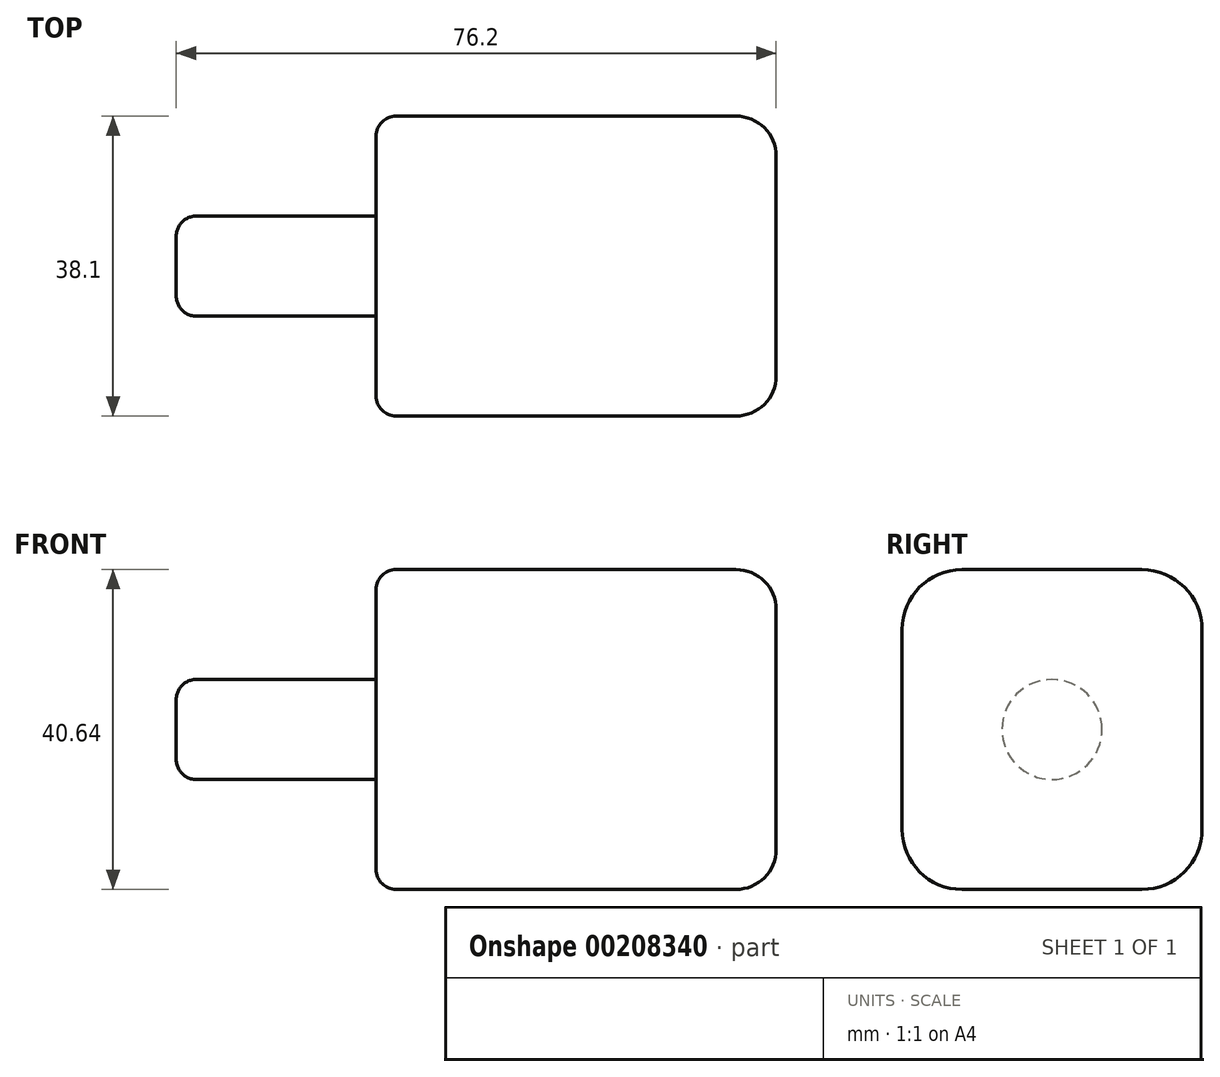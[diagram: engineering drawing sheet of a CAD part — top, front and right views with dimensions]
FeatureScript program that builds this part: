
annotation { "Feature Type Name" : "Feature", "Feature Type Description" : "" }
export const myFeature = defineFeature(function(context is Context, id is Id, definition is map)
    precondition{}
    {
        {
            var Q0;
            Q0=qCreatedBy(makeId("Right.planeOp"),FACE);
            var sketch = newSketch(context, id + "F0", { "sketchPlane" : qUnion([Q0])});
            skLineSegment(sketch, "E0.bottom", {"start": v(-15.1, 19.7) * mm, "end": v(23, 19.7) * mm});
            skLineSegment(sketch, "E0.top", {"start": v(-15.1, -20.93) * mm, "end": v(23, -20.93) * mm});
            skLineSegment(sketch, "E0.left", {"start": v(-15.1, 19.7) * mm, "end": v(-15.1, -20.93) * mm});
            skLineSegment(sketch, "E0.right", {"start": v(23, 19.7) * mm, "end": v(23, -20.93) * mm});
            skSolve(sketch);
        }
        {
            var Q0;
            Q0=makeQuery(id+"F0.imprint","IMPRINT",FACE,{"disambiguationData":[TD([[makeQuery(id+"F0.imprint","IMPRINT",EDGE,{"derivedFrom":sQuery(id+"F0.wireOp",EDGE,"E0.bottom")}),-1.0]])]});
            extrude(context, id + "F1", {"entities" : qUnion([Q0]), "depth" : 50.8 * mm});
        }
        {
            var Q0;
            Q0=makeQuery(id+"F1.opExtrude","CAP_FACE",FACE,{"disambiguationData":[OSD([sQuery(id+"F0.wireOp",EDGE,"E0.bottom"),sQuery(id+"F0.wireOp",EDGE,"E0.top"),sQuery(id+"F0.wireOp",EDGE,"E0.left"),sQuery(id+"F0.wireOp",EDGE,"E0.right")])],"isStart":true});
            var sketch = newSketch(context, id + "F2", { "sketchPlane" : qUnion([Q0])});
            skLineSegment(sketch, "E1", {"start": v(-23, -0.61) * mm, "end": v(15.1, -0.61) * mm});
            skLineSegment(sketch, "E2", {"start": v(-3.96, 19.7) * mm, "end": v(-3.96, -20.93) * mm});
            skCircle(sketch, "E3", {"center": v(-3.96, -0.61) * mm, "radius": 6.35 * mm});
            skSolve(sketch);
        }
        {
            var Q0;
            {var subQ0=sQuery(id+"F2.wireOp",EDGE,"E3");var subQ1=sQuery(id+"F2.wireOp",EDGE,"E1");var subQ2=makeQuery(id+"F2.imprint","INTERSECT",VERTEX,{"disambiguationData":[OD(0.0)],"derivedFrom":[subQ1,subQ0]});Q0=makeQuery(id+"F2.imprint","IMPRINT",FACE,{"disambiguationData":[TD([[makeQuery(id+"F2.imprint","IMPRINT",EDGE,{"disambiguationData":[TD([[subQ2,-1.0]])],"derivedFrom":subQ1}),-1.0]])]});}
            var Q1;
            {var subQ0=sQuery(id+"F2.wireOp",EDGE,"E2");var subQ1=sQuery(id+"F2.wireOp",EDGE,"E1");var subQ2=makeQuery(id+"F2.imprint","INTERSECT",VERTEX,{"derivedFrom":[subQ1,subQ0]});Q1=makeQuery(id+"F2.imprint","IMPRINT",FACE,{"disambiguationData":[TD([[makeQuery(id+"F2.imprint","IMPRINT",EDGE,{"disambiguationData":[TD([[subQ2,-1.0]])],"derivedFrom":subQ1}),-1.0]])]});}
            var Q2;
            {var subQ0=sQuery(id+"F2.wireOp",EDGE,"E3");var subQ1=sQuery(id+"F2.wireOp",EDGE,"E1");var subQ2=makeQuery(id+"F2.imprint","INTERSECT",VERTEX,{"disambiguationData":[OD(0.0)],"derivedFrom":[subQ1,subQ0]});Q2=makeQuery(id+"F2.imprint","IMPRINT",FACE,{"disambiguationData":[TD([[makeQuery(id+"F2.imprint","IMPRINT",EDGE,{"disambiguationData":[TD([[subQ2,-1.0]])],"derivedFrom":subQ1}),1.0]])]});}
            var Q3;
            {var subQ0=sQuery(id+"F2.wireOp",EDGE,"E2");var subQ1=sQuery(id+"F2.wireOp",EDGE,"E1");var subQ2=makeQuery(id+"F2.imprint","INTERSECT",VERTEX,{"derivedFrom":[subQ1,subQ0]});Q3=makeQuery(id+"F2.imprint","IMPRINT",FACE,{"disambiguationData":[TD([[makeQuery(id+"F2.imprint","IMPRINT",EDGE,{"disambiguationData":[TD([[subQ2,-1.0]])],"derivedFrom":subQ1}),1.0]])]});}
            extrude(context, id + "F3", {"entities" : qUnion([Q0, Q1, Q2, Q3]), "operationType" : NewBodyOperationType.ADD, "depth" : 25.4 * mm});
        }
        {
            var Q0;
            Q0=makeQuery(id+"F1.opExtrude","SWEPT_EDGE",EDGE,{"disambiguationData":[OSD([sQuery(id+"F0.wireOp",EDGE,"E0.top"),sQuery(id+"F0.wireOp",EDGE,"E0.right")])]});
            var Q1;
            Q1=makeQuery(id+"F1.opExtrude","SWEPT_EDGE",EDGE,{"disambiguationData":[OSD([sQuery(id+"F0.wireOp",EDGE,"E0.top"),sQuery(id+"F0.wireOp",EDGE,"E0.left")])]});
            var Q2;
            Q2=makeQuery(id+"F1.opExtrude","SWEPT_EDGE",EDGE,{"disambiguationData":[OSD([sQuery(id+"F0.wireOp",EDGE,"E0.bottom"),sQuery(id+"F0.wireOp",EDGE,"E0.left")])]});
            var Q3;
            Q3=makeQuery(id+"F1.opExtrude","SWEPT_EDGE",EDGE,{"disambiguationData":[OSD([sQuery(id+"F0.wireOp",EDGE,"E0.bottom"),sQuery(id+"F0.wireOp",EDGE,"E0.right")])]});
            fillet(context, id + "F4", {"entities" : qUnion([Q0, Q1, Q2, Q3]), "radius" : 7.62 * mm, "tangentPropagation" : true, "allowEdgeOverflow" : false});
        }
        {
            var Q0;
            Q0=makeQuery(id+"F1.opExtrude","CAP_EDGE",EDGE,{"disambiguationData":[OSD([sQuery(id+"F0.wireOp",EDGE,"E0.top")])],"isStart":true});
            fillet(context, id + "F5", {"entities" : qUnion([Q0]), "radius" : 2.54 * mm, "tangentPropagation" : true, "allowEdgeOverflow" : false});
        }
        {
            var Q0;
            Q0=makeQuery(id+"F3.opExtrude","CAP_FACE",FACE,{"disambiguationData":[OSD([sQuery(id+"F2.wireOp",EDGE,"E3")])],"isStart":false});
            fillet(context, id + "F6", {"entities" : qUnion([Q0]), "radius" : 2.54 * mm, "tangentPropagation" : true, "allowEdgeOverflow" : false});
        }
        {
            var Q0;
            Q0=makeQuery(id+"F1.opExtrude","CAP_EDGE",EDGE,{"disambiguationData":[OSD([sQuery(id+"F0.wireOp",EDGE,"E0.bottom")])],"isStart":false});
            var Q1;
            {var subQ0=sQuery(id+"F0.wireOp",EDGE,"E0.left");var subQ1=sQuery(id+"F0.wireOp",EDGE,"E0.bottom");Q1=makeQuery(id+"F4.opFillet","BLEND_EDGE",EDGE,{"blendedFrom":[makeQuery(id+"F1.opExtrude","SWEPT_EDGE",EDGE,{"disambiguationData":[OSD([subQ1,subQ0])]}),makeQuery(id+"F1.opExtrude","CAP_FACE",FACE,{"disambiguationData":[OSD([subQ1,sQuery(id+"F0.wireOp",EDGE,"E0.top"),subQ0,sQuery(id+"F0.wireOp",EDGE,"E0.right")])],"isStart":false})],"blendedInto":[makeQuery(id+"F1.opExtrude","CAP_FACE",FACE,{"disambiguationData":[OSD([subQ1,sQuery(id+"F0.wireOp",EDGE,"E0.top"),subQ0,sQuery(id+"F0.wireOp",EDGE,"E0.right")])],"isStart":false})]});}
            var Q2;
            Q2=makeQuery(id+"F1.opExtrude","CAP_EDGE",EDGE,{"disambiguationData":[OSD([sQuery(id+"F0.wireOp",EDGE,"E0.left")])],"isStart":false});
            var Q3;
            {var subQ0=sQuery(id+"F0.wireOp",EDGE,"E0.left");var subQ1=sQuery(id+"F0.wireOp",EDGE,"E0.top");Q3=makeQuery(id+"F4.opFillet","BLEND_EDGE",EDGE,{"blendedFrom":[makeQuery(id+"F1.opExtrude","SWEPT_EDGE",EDGE,{"disambiguationData":[OSD([subQ1,subQ0])]}),makeQuery(id+"F1.opExtrude","CAP_FACE",FACE,{"disambiguationData":[OSD([sQuery(id+"F0.wireOp",EDGE,"E0.bottom"),subQ1,subQ0,sQuery(id+"F0.wireOp",EDGE,"E0.right")])],"isStart":false})],"blendedInto":[makeQuery(id+"F1.opExtrude","CAP_FACE",FACE,{"disambiguationData":[OSD([sQuery(id+"F0.wireOp",EDGE,"E0.bottom"),subQ1,subQ0,sQuery(id+"F0.wireOp",EDGE,"E0.right")])],"isStart":false})]});}
            var Q4;
            Q4=makeQuery(id+"F1.opExtrude","CAP_EDGE",EDGE,{"disambiguationData":[OSD([sQuery(id+"F0.wireOp",EDGE,"E0.top")])],"isStart":false});
            var Q5;
            Q5=makeQuery(id+"F1.opExtrude","CAP_EDGE",EDGE,{"disambiguationData":[OSD([sQuery(id+"F0.wireOp",EDGE,"E0.right")])],"isStart":false});
            var Q6;
            {var subQ0=sQuery(id+"F0.wireOp",EDGE,"E0.right");var subQ1=sQuery(id+"F0.wireOp",EDGE,"E0.bottom");Q6=makeQuery(id+"F4.opFillet","BLEND_EDGE",EDGE,{"blendedFrom":[makeQuery(id+"F1.opExtrude","SWEPT_EDGE",EDGE,{"disambiguationData":[OSD([subQ1,subQ0])]}),makeQuery(id+"F1.opExtrude","CAP_FACE",FACE,{"disambiguationData":[OSD([subQ1,sQuery(id+"F0.wireOp",EDGE,"E0.top"),sQuery(id+"F0.wireOp",EDGE,"E0.left"),subQ0])],"isStart":false})],"blendedInto":[makeQuery(id+"F1.opExtrude","CAP_FACE",FACE,{"disambiguationData":[OSD([subQ1,sQuery(id+"F0.wireOp",EDGE,"E0.top"),sQuery(id+"F0.wireOp",EDGE,"E0.left"),subQ0])],"isStart":false})]});}
            var Q7;
            {var subQ0=sQuery(id+"F0.wireOp",EDGE,"E0.right");var subQ1=sQuery(id+"F0.wireOp",EDGE,"E0.top");Q7=makeQuery(id+"F4.opFillet","BLEND_EDGE",EDGE,{"blendedFrom":[makeQuery(id+"F1.opExtrude","SWEPT_EDGE",EDGE,{"disambiguationData":[OSD([subQ1,subQ0])]}),makeQuery(id+"F1.opExtrude","CAP_FACE",FACE,{"disambiguationData":[OSD([sQuery(id+"F0.wireOp",EDGE,"E0.bottom"),subQ1,sQuery(id+"F0.wireOp",EDGE,"E0.left"),subQ0])],"isStart":false})],"blendedInto":[makeQuery(id+"F1.opExtrude","CAP_FACE",FACE,{"disambiguationData":[OSD([sQuery(id+"F0.wireOp",EDGE,"E0.bottom"),subQ1,sQuery(id+"F0.wireOp",EDGE,"E0.left"),subQ0])],"isStart":false})]});}
            fillet(context, id + "F7", {"entities" : qUnion([Q0, Q1, Q2, Q3, Q4, Q5, Q6, Q7]), "radius" : 5.08 * mm, "tangentPropagation" : true, "allowEdgeOverflow" : false});
        }
    });
